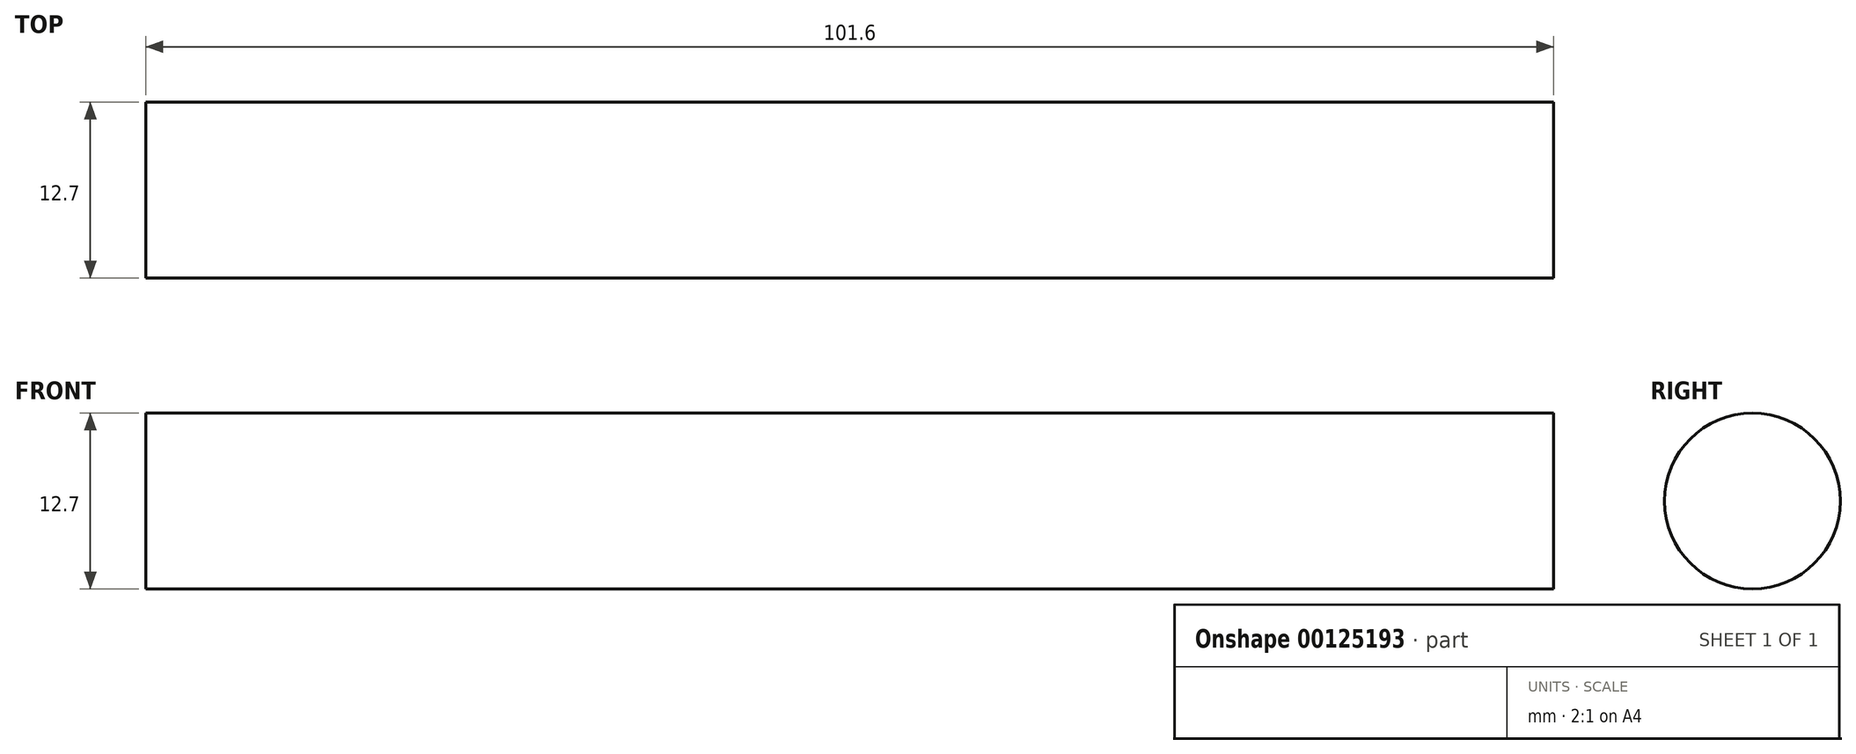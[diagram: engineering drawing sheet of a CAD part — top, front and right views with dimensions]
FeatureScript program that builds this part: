
annotation { "Feature Type Name" : "Feature", "Feature Type Description" : "" }
export const myFeature = defineFeature(function(context is Context, id is Id, definition is map)
    precondition{}
    {
        {
            var Q0;
            Q0=qCreatedBy(makeId("Front.planeOp"),FACE);
            var sketch = newSketch(context, id + "F0", { "sketchPlane" : qUnion([Q0])});
            skLineSegment(sketch, "E0.bottom", {"start": v(-50.8, 0) * mm, "end": v(50.8, 0) * mm});
            skLineSegment(sketch, "E0.top", {"start": v(-50.8, -6.35) * mm, "end": v(50.8, -6.35) * mm});
            skLineSegment(sketch, "E0.left", {"start": v(-50.8, 0) * mm, "end": v(-50.8, -6.35) * mm});
            skLineSegment(sketch, "E0.right", {"start": v(50.8, 0) * mm, "end": v(50.8, -6.35) * mm});
            skPoint(sketch, "E1.endSnap0", {"position": v(0, 0) * mm});
            skLineSegment(sketch, "E2", {"start": v(-50.8, -6.35) * mm, "end": v(50.8, -6.35) * mm, "construction": true});
            skLineSegment(sketch, "E3", {"start": v(-50.8, 0) * mm, "end": v(-163.56, 0) * mm, "construction": true});
            skSolve(sketch);
        }
        {
            var Q0;
            Q0=qSketchRegion(id+"F0",true);
            var Q1;
            Q1=sQuery(id+"F0.wireOp",EDGE,"E3");
            revolve(context, id + "F1", {"entities" : qUnion([Q0]), "axis" : qUnion([Q1]), "revolveType" : RevolveType.FULL});
        }
    });
